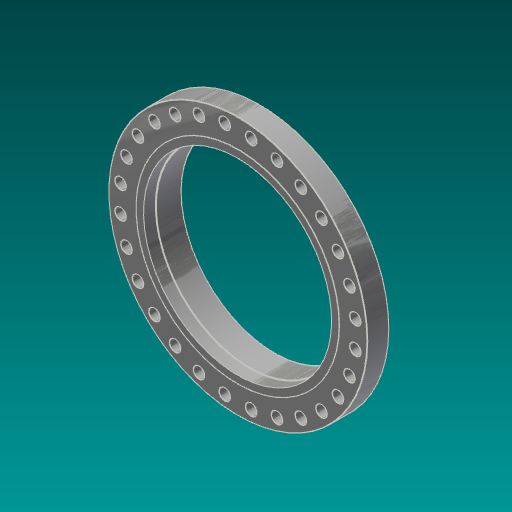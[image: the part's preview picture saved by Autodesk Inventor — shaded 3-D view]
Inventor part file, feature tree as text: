
AUTODESK INVENTOR PART (.ipt)
format: ipt  version: 2017.3 (Build 213256000, 256)  size: 376,832 bytes
history: native  units: in
note: dims shown in document units (in); Inventor stores cm internally (conversion verified against a paired STEP export)
features: sketch x5, extrude x3, chamfer x3, fillet x2, hole x1, pattern_circular x1, revolve x1
ambient origin geometry x8: Origin, YZ Plane, XZ Plane, XY Plane, X Axis, Y Axis, Z Axis, Center Point
bodies: Solid1 (feature_tree)
feature tree (16):
  extrude  "Extrusion1"  Depth=31.0in
  extrude  "Extrusion2"  Depth=3.625in
  extrude  "Extrusion3"  Depth=0.0625in
  hole  "Hole1"  [1 undecoded]
  chamfer  "Chamfer3"  Distance=11.0236in Angle=360.0deg
  pattern_circular  "Circular Pattern1"  [2 undecoded]
  chamfer  "Chamfer2"  Distance=0.4375in
  fillet  "Fillet2"  Radius=0.0312in
  chamfer  "Chamfer4"  Distance=0.0625in Angle=45.0deg
  revolve  "Revolution1"  Angle=90.0deg
  fillet  "Fillet5"  Radius=2.0in
  sketch  "Sketch1"  dims[d0=43.0in d1=31.0in]
  sketch  "Sketch2"  dims[d2=3.625in d3=0.0in d4=33.75in]
  sketch  "Sketch3"  dims[d5=0.0625in d6=0.0in d7=34.75in]
  sketch  "Sketch4"  dims[d8=2.4375in d9=0.0in d13=19.625in]
  sketch  "Sketch6"  dims[d14=0.0442in d15=1.875in d16=0.75in d17=0.375in d18=0.25in d19=0.5635in d20=1.0in d21=0.8108in d22=11.0236in d23=360.0deg d25=0.0625in d26=0.125in d27=0.0687in d29=0.4375in d30=0.0312in d31=0.125in d32=45.0deg d33=0.0625in d34=0.125in d35=45.0deg d49=90.0deg d71=2.0in d72=15.625in d73=0.0312in d94=16.0in d95=0.4375in d96=0.2577in d99=0.5in d100=0.625in d101=0.2893in]
note: 3 required parameter values undecoded (feature->parameter linkage not recoverable at this tier; creation-order binding heuristic only, values carry confidence <= 0.55)
